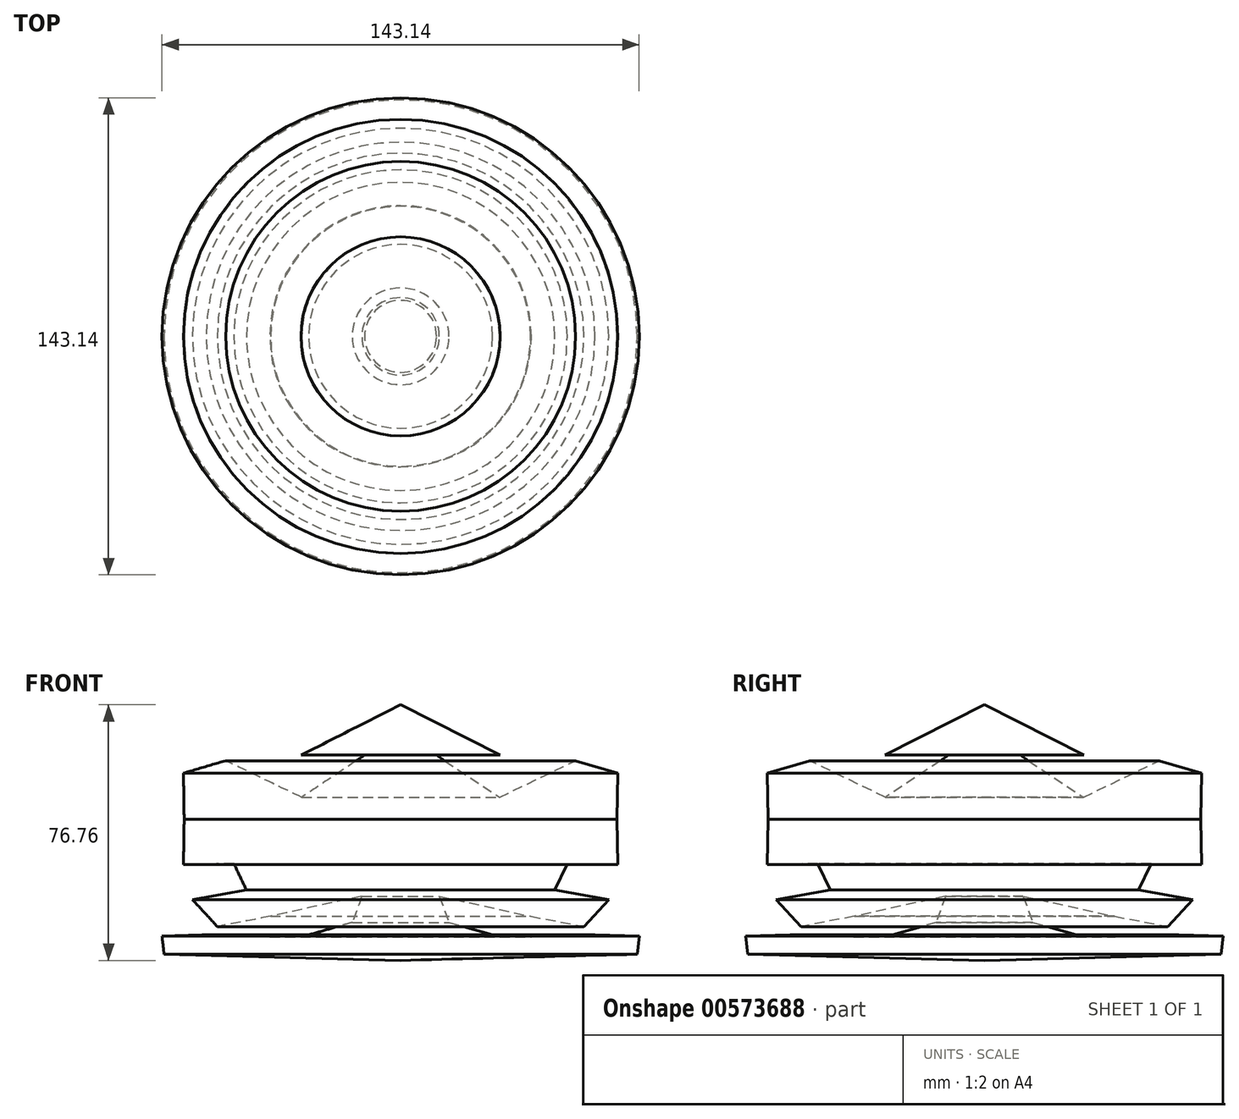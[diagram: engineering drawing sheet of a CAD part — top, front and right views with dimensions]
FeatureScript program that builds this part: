
annotation { "Feature Type Name" : "Feature", "Feature Type Description" : "" }
export const myFeature = defineFeature(function(context is Context, id is Id, definition is map)
    precondition{}
    {
        {
            var Q0;
            Q0=qCreatedBy(makeId("Front.planeOp"),FACE);
            var sketch = newSketch(context, id + "F0", { "sketchPlane" : qUnion([Q0])});
            skLineSegment(sketch, "E0", {"start": v(0, 76.76) * mm, "end": v(29.87, 61.61) * mm});
            skLineSegment(sketch, "E1", {"start": v(29.87, 61.61) * mm, "end": v(10.79, 61.61) * mm});
            skLineSegment(sketch, "E2", {"start": v(10.79, 61.61) * mm, "end": v(29.67, 48.96) * mm});
            skLineSegment(sketch, "E3", {"start": v(29.67, 48.96) * mm, "end": v(52.49, 59.96) * mm});
            skLineSegment(sketch, "E4", {"start": v(52.49, 59.96) * mm, "end": v(65.14, 56.22) * mm});
            skLineSegment(sketch, "E5", {"start": v(65.14, 56.22) * mm, "end": v(64.93, 42.32) * mm});
            skLineSegment(sketch, "E6", {"start": v(64.93, 42.32) * mm, "end": v(65.14, 28.84) * mm});
            skLineSegment(sketch, "E7", {"start": v(65.14, 28.84) * mm, "end": v(50, 29.04) * mm});
            skLineSegment(sketch, "E8", {"start": v(50, 29.04) * mm, "end": v(46.26, 21.16) * mm});
            skLineSegment(sketch, "E9", {"start": v(46.26, 21.16) * mm, "end": v(62.44, 18.26) * mm});
            skLineSegment(sketch, "E10", {"start": v(62.44, 18.26) * mm, "end": v(54.98, 10.17) * mm});
            skLineSegment(sketch, "E11", {"start": v(54.98, 10.17) * mm, "end": v(39, 13.28) * mm});
            skLineSegment(sketch, "E12", {"start": v(39, 13.28) * mm, "end": v(11.62, 19.3) * mm});
            skLineSegment(sketch, "E13", {"start": v(11.62, 19.3) * mm, "end": v(14.52, 11.41) * mm});
            skLineSegment(sketch, "E14", {"start": v(14.52, 11.41) * mm, "end": v(27.6, 7.68) * mm});
            skLineSegment(sketch, "E15", {"start": v(27.6, 7.68) * mm, "end": v(39.2, 7.05) * mm});
            skLineSegment(sketch, "E16", {"start": v(39.2, 7.05) * mm, "end": v(58.3, 7.68) * mm});
            skLineSegment(sketch, "E17", {"start": v(58.3, 7.68) * mm, "end": v(71.57, 7.26) * mm});
            skLineSegment(sketch, "E18", {"start": v(71.57, 7.26) * mm, "end": v(70.95, 1.87) * mm});
            skLineSegment(sketch, "E19", {"start": v(70.95, 1.87) * mm, "end": v(0, 0) * mm});
            skLineSegment(sketch, "E20", {"start": v(0, 0) * mm, "end": v(0, 76.76) * mm});
            skSolve(sketch);
        }
        {
            var Q0;
            Q0 = qSketchRegion(id + "F0", true);
            var Q1;
            Q1=sQuery(id+"F0.wireOp",EDGE,"E20");
            revolve(context, id + "F1", {"entities" : qUnion([Q0]), "axis" : qUnion([Q1]), "revolveType" : RevolveType.FULL});
        }
    });
